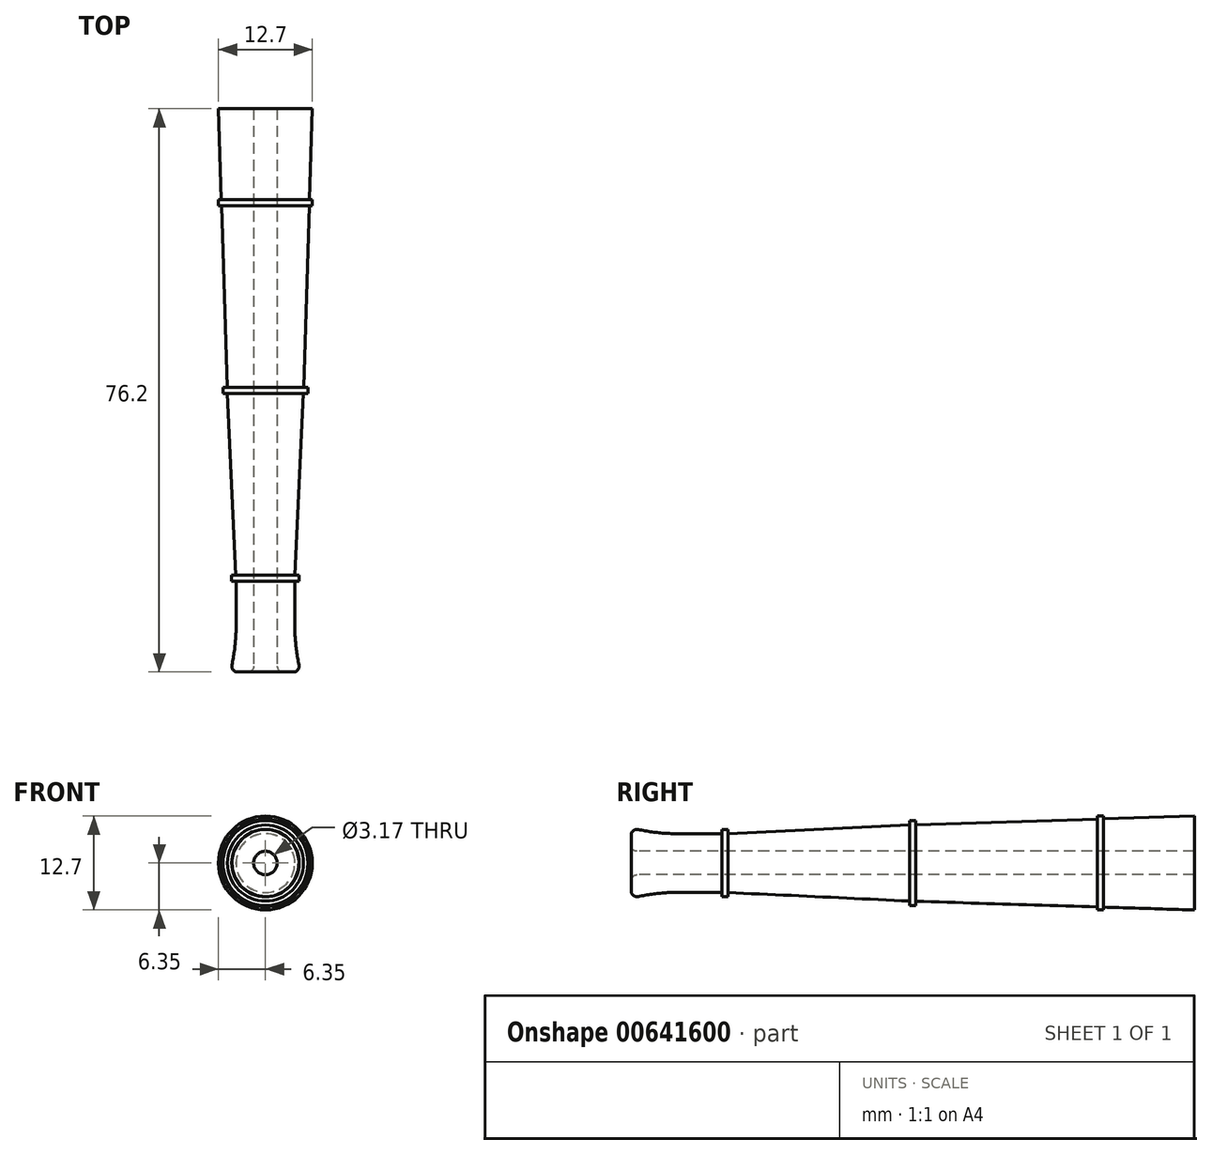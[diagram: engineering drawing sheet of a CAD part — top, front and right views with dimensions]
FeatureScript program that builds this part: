
annotation { "Feature Type Name" : "Feature", "Feature Type Description" : "" }
export const myFeature = defineFeature(function(context is Context, id is Id, definition is map)
    precondition{}
    {
        {
            var Q0;
            Q0=qCreatedBy(makeId("Right.planeOp"),FACE);
            var sketch = newSketch(context, id + "F0", { "sketchPlane" : qUnion([Q0])});
            skLineSegment(sketch, "E0", {"start": v(0, 0) * mm, "end": v(76.2, 0) * mm, "construction": true});
            skLineSegment(sketch, "E1", {"start": v(76.2, 0) * mm, "end": v(76.2, 1.59) * mm, "construction": true});
            skLineSegment(sketch, "E2", {"start": v(76.2, 1.59) * mm, "end": v(76.2, 6.35) * mm});
            skLineSegment(sketch, "E3", {"start": v(76.2, 1.59) * mm, "end": v(0, 1.59) * mm});
            skLineSegment(sketch, "E4", {"start": v(0, 1.59) * mm, "end": v(0, 0) * mm, "construction": true});
            skLineSegment(sketch, "E5", {"start": v(0, 1.59) * mm, "end": v(0, 4.76) * mm});
            skLineSegment(sketch, "E6", {"start": v(0, 4.76) * mm, "end": v(76.2, 6.35) * mm, "construction": true});
            skLineSegment(sketch, "E7", {"start": v(0, 3.97) * mm, "end": v(76.2, 3.97) * mm, "construction": true});
            skLineSegment(sketch, "E8", {"start": v(63.1, 6.35) * mm, "end": v(63.9, 6.35) * mm});
            skLineSegment(sketch, "E9", {"start": v(38.5, 5.75) * mm, "end": v(37.7, 5.75) * mm});
            skLineSegment(sketch, "E10", {"start": v(12.3, 4.56) * mm, "end": v(13.1, 4.56) * mm});
            skLineSegment(sketch, "E11", {"start": v(63.5, 5.95) * mm, "end": v(76.2, 6.35) * mm});
            skLineSegment(sketch, "E12", {"start": v(63.9, 6.35) * mm, "end": v(63.9, 1.59) * mm});
            skLineSegment(sketch, "E13", {"start": v(63.1, 6.35) * mm, "end": v(63.1, 1.59) * mm});
            skLineSegment(sketch, "E14", {"start": v(63.5, 6.35) * mm, "end": v(63.5, 0) * mm, "construction": true});
            skLineSegment(sketch, "E15", {"start": v(38.5, 5.75) * mm, "end": v(38.5, 1.59) * mm});
            skLineSegment(sketch, "E16", {"start": v(37.7, 5.75) * mm, "end": v(37.7, 1.59) * mm});
            skLineSegment(sketch, "E17", {"start": v(38.1, 5.75) * mm, "end": v(38.1, 0) * mm, "construction": true});
            skLineSegment(sketch, "E18", {"start": v(12.7, 4.56) * mm, "end": v(12.7, 0) * mm, "construction": true});
            skLineSegment(sketch, "E19", {"start": v(13.1, 4.56) * mm, "end": v(13.1, 1.59) * mm});
            skLineSegment(sketch, "E20", {"start": v(12.3, 4.56) * mm, "end": v(12.3, 1.59) * mm});
            skLineSegment(sketch, "E21", {"start": v(38.1, 5.16) * mm, "end": v(63.5, 5.95) * mm});
            skLineSegment(sketch, "E22", {"start": v(38.1, 5.16) * mm, "end": v(12.7, 3.97) * mm});
            skLineSegment(sketch, "E23", {"start": v(6.35, 3.97) * mm, "end": v(12.7, 3.97) * mm});
            skArc(sketch, "E24", {"start": v(0, 4.76) * mm, "mid": v(3.15, 4.17) * mm, "end": v(6.35, 3.97) * mm});
            skSolve(sketch);
        }
        {
            var Q0;
            {var subQ0=sQuery(id+"F0.wireOp",EDGE,"E5");Q0=makeQuery(id+"F0.imprint","IMPRINT",FACE,{"disambiguationData":[TD([[makeQuery(id+"F0.imprint","IMPRINT",EDGE,{"derivedFrom":subQ0}),-1.0]])]});}
            var Q1;
            {var subQ1=sQuery(id+"F0.wireOp",EDGE,"E3");var subQ5=sQuery(id+"F0.wireOp",EDGE,"E19");var subQ6=makeQuery(id+"F0.imprint","INTERSECT",VERTEX,{"derivedFrom":[subQ1,subQ5]});Q1=makeQuery(id+"F0.imprint","IMPRINT",FACE,{"disambiguationData":[TD([[makeQuery(id+"F0.imprint","IMPRINT",EDGE,{"disambiguationData":[TD([[subQ6,-1.0]])],"derivedFrom":subQ1}),-1.0]])]});}
            var Q2;
            {var subQ1=sQuery(id+"F0.wireOp",EDGE,"E10");Q2=makeQuery(id+"F0.imprint","IMPRINT",FACE,{"disambiguationData":[TD([[makeQuery(id+"F0.imprint","IMPRINT",EDGE,{"derivedFrom":subQ1}),-1.0]])]});}
            var Q3;
            {var subQ0=sQuery(id+"F0.wireOp",EDGE,"E16");var subQ1=sQuery(id+"F0.wireOp",EDGE,"E3");var subQ2=makeQuery(id+"F0.imprint","INTERSECT",VERTEX,{"derivedFrom":[subQ1,subQ0]});Q3=makeQuery(id+"F0.imprint","IMPRINT",FACE,{"disambiguationData":[TD([[makeQuery(id+"F0.imprint","IMPRINT",EDGE,{"disambiguationData":[TD([[subQ2,-1.0]])],"derivedFrom":subQ1}),-1.0]])]});}
            var Q4;
            {var subQ3=sQuery(id+"F0.wireOp",EDGE,"E15");var subQ6=sQuery(id+"F0.wireOp",EDGE,"E3");var subQ9=makeQuery(id+"F0.imprint","INTERSECT",VERTEX,{"derivedFrom":[subQ6,subQ3]});Q4=makeQuery(id+"F0.imprint","IMPRINT",FACE,{"disambiguationData":[TD([[makeQuery(id+"F0.imprint","IMPRINT",EDGE,{"disambiguationData":[TD([[subQ9,-1.0]])],"derivedFrom":subQ6}),-1.0]])]});}
            var Q5;
            {var subQ5=sQuery(id+"F0.wireOp",EDGE,"E9");Q5=makeQuery(id+"F0.imprint","IMPRINT",FACE,{"disambiguationData":[TD([[makeQuery(id+"F0.imprint","IMPRINT",EDGE,{"derivedFrom":subQ5}),1.0]])]});}
            var Q6;
            {var subQ0=sQuery(id+"F0.wireOp",EDGE,"E13");var subQ1=sQuery(id+"F0.wireOp",EDGE,"E3");var subQ2=makeQuery(id+"F0.imprint","INTERSECT",VERTEX,{"derivedFrom":[subQ1,subQ0]});Q6=makeQuery(id+"F0.imprint","IMPRINT",FACE,{"disambiguationData":[TD([[makeQuery(id+"F0.imprint","IMPRINT",EDGE,{"disambiguationData":[TD([[subQ2,-1.0]])],"derivedFrom":subQ1}),-1.0]])]});}
            var Q7;
            {var subQ0=sQuery(id+"F0.wireOp",EDGE,"E2");Q7=makeQuery(id+"F0.imprint","IMPRINT",FACE,{"disambiguationData":[TD([[makeQuery(id+"F0.imprint","IMPRINT",EDGE,{"derivedFrom":subQ0}),1.0]])]});}
            var Q8;
            {var subQ1=sQuery(id+"F0.wireOp",EDGE,"E3");var subQ7=sQuery(id+"F0.wireOp",EDGE,"E12");var subQ9=makeQuery(id+"F0.imprint","INTERSECT",VERTEX,{"derivedFrom":[subQ1,subQ7]});Q8=makeQuery(id+"F0.imprint","IMPRINT",FACE,{"disambiguationData":[TD([[makeQuery(id+"F0.imprint","IMPRINT",EDGE,{"disambiguationData":[TD([[subQ9,-1.0]])],"derivedFrom":subQ1}),-1.0]])]});}
            var Q9;
            {var subQ1=sQuery(id+"F0.wireOp",EDGE,"E8");Q9=makeQuery(id+"F0.imprint","IMPRINT",FACE,{"disambiguationData":[TD([[makeQuery(id+"F0.imprint","IMPRINT",EDGE,{"derivedFrom":subQ1}),-1.0]])]});}
            var Q10;
            Q10=sQuery(id+"F0.wireOp",EDGE,"E0");
            revolve(context, id + "F1", {"entities" : qUnion([Q0, Q1, Q2, Q3, Q4, Q5, Q6, Q7, Q8, Q9]), "axis" : qUnion([Q10]), "revolveType" : RevolveType.FULL});
        }
        {
            var Q0;
            Q0=makeQuery(id+"F1.opRevolve","SWEPT_EDGE",EDGE,{"disambiguationData":[OSD([sQuery(id+"F0.wireOp",EDGE,"E5"),sQuery(id+"F0.wireOp",EDGE,"b4e7f3d7-f4b2-4b89-927e-fea6c5432f28")])]});
            fillet(context, id + "F2", {"entities" : qUnion([Q0]), "radius" : 0.8 * mm, "tangentPropagation" : true, "allowEdgeOverflow" : false});
        }
    });
